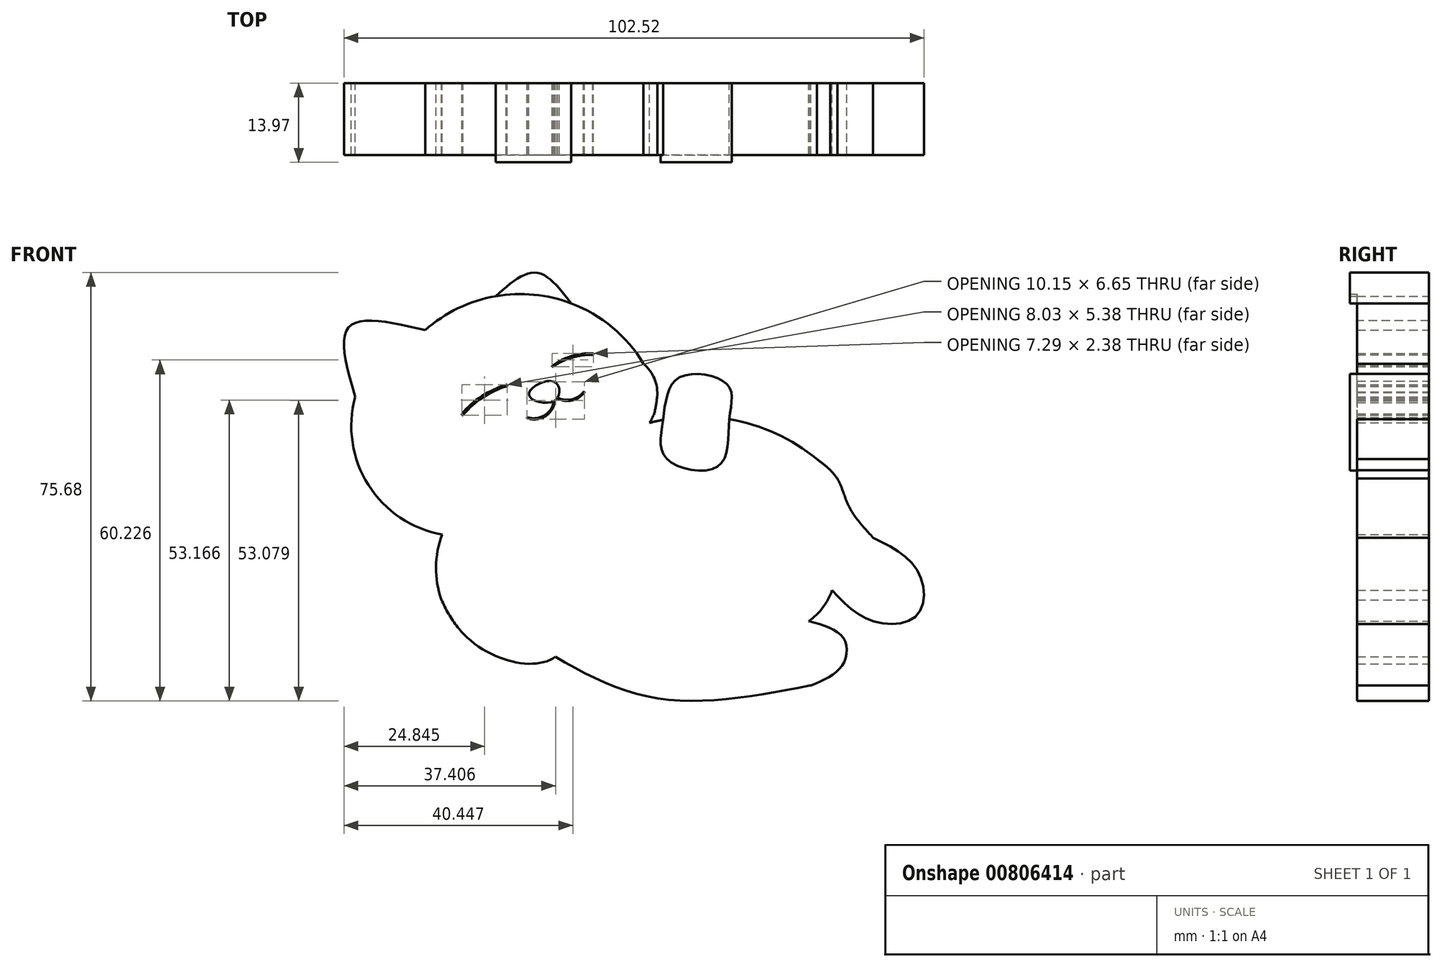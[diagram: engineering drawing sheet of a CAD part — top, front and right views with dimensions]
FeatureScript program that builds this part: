
annotation { "Feature Type Name" : "Feature", "Feature Type Description" : "" }
export const myFeature = defineFeature(function(context is Context, id is Id, definition is map)
    precondition{}
    {
        {
            var Q0;
            Q0=qCreatedBy(makeId("Front.planeOp"),FACE);
            var sketch = newSketch(context, id + "F0", { "sketchPlane" : qUnion([Q0])});
            skArc(sketch, "E0", {"start": v(56.76, -2.28) * mm, "mid": v(49.48, 2.28) * mm, "end": v(41.27, 4.8) * mm});
            skArc(sketch, "E1", {"start": v(59.42, -25.44) * mm, "mid": v(59.84, -24) * mm, "end": v(60.01, -22.52) * mm});
            skFitSpline(sketch, "E2", {"points": [v(55.5, -42.26) * mm, v(27.75, -44.4) * mm, v(5.04, -33.79) * mm], "startDerivative": vector(-56, -10.82) * mm, "endDerivative": vector(-44.82, 28.1) * mm});
            skFitSpline(sketch, "E3", {"points": [v(29.53, 4.68) * mm, v(30.27, -2.25) * mm, v(39.28, -3.51) * mm, v(41.27, 4.8) * mm, v(40.9, 10.9) * mm, v(32.43, 12.16) * mm, v(29.53, 4.68) * mm]});
            skArc(sketch, "E4", {"start": v(41.27, 4.8) * mm, "mid": v(35.37, 8.1) * mm, "end": v(29.53, 4.68) * mm});
            skPoint(sketch, "E5", {"position": v(-11.24, -21.98) * mm});
            skPoint(sketch, "E6", {"position": v(24.84, 3.42) * mm});
            skArc(sketch, "E7.trimOffspring", {"start": v(29.53, 4.68) * mm, "mid": v(27.16, 4.14) * mm, "end": v(24.84, 3.42) * mm});
            skPoint(sketch, "E8", {"position": v(6.4, -24.5) * mm});
            skPoint(sketch, "E9.3.internal.orphan", {"position": v(55.68, -42.26) * mm});
            skPoint(sketch, "E9.endDerivative.orphan", {"position": v(60.74, -44.4) * mm});
            skPoint(sketch, "E9.startDerivative.orphan", {"position": v(60.44, -32.16) * mm});
            skPoint(sketch, "E10.3.internal.orphan", {"position": v(66.67, -30.9) * mm});
            skFitSpline(sketch, "E11", {"points": [v(59.42, -25.44) * mm, v(66.67, -30.9) * mm, v(74.55, -29.7) * mm, v(74.55, -22.05) * mm, v(66.67, -16.13) * mm], "startDerivative": vector(25.1, -26.33) * mm, "endDerivative": vector(-35.3, 17.66) * mm});
            skFitSpline(sketch, "E12", {"points": [v(55.68, -42.26) * mm, v(61.18, -38.75) * mm, v(61.43, -33.9) * mm, v(54.9, -30.8) * mm], "startDerivative": vector(19.1, 8) * mm, "endDerivative": vector(-22.54, 5.93) * mm});
            skFitSpline(sketch, "E13", {"points": [v(66.67, -16.13) * mm, v(62.44, -10.72) * mm, v(60.34, -5.7) * mm, v(56.76, -2.28) * mm], "startDerivative": vector(-13.38, 14.34) * mm, "endDerivative": vector(-13.07, 9.95) * mm});
            skArc(sketch, "E14", {"start": v(62.44, -10.72) * mm, "mid": v(60.48, -5.9) * mm, "end": v(56.76, -2.28) * mm});
            skArc(sketch, "E15", {"start": v(52.98, -32.16) * mm, "mid": v(56.92, -29.5) * mm, "end": v(59.42, -25.44) * mm});
            skPoint(sketch, "E16.orphan", {"position": v(55.68, -30) * mm});
            skPoint(sketch, "E17", {"position": v(60.01, -22.52) * mm});
            skArc(sketch, "E18", {"start": v(-24.86, 8.73) * mm, "mid": v(-22.52, -6.83) * mm, "end": v(-9.46, -15.6) * mm});
            skFitSpline(sketch, "E19", {"points": [v(-24.86, 8.73) * mm, v(-25.93, 21.14) * mm, v(-12.5, 20.53) * mm], "startDerivative": vector(-9.2, 31.8) * mm, "endDerivative": vector(33.64, -7.95) * mm});
            skArc(sketch, "E20", {"start": v(17.84, 0) * mm, "mid": v(21.55, 1.28) * mm, "end": v(24.84, 3.42) * mm});
            skArc(sketch, "E21", {"start": v(28.49, 8.68) * mm, "mid": v(28.04, 11.94) * mm, "end": v(26.1, 14.6) * mm});
            skArc(sketch, "E22.trimOffspring", {"start": v(26.1, 14.6) * mm, "mid": v(8.19, 26.61) * mm, "end": v(-12.5, 20.53) * mm});
            skFitSpline(sketch, "E23", {"points": [v(28.49, 8.68) * mm, v(27.16, 4.14) * mm, v(16.83, -4.76) * mm], "startDerivative": vector(-1.19, -11.9) * mm, "endDerivative": vector(-20.46, -14.73) * mm});
            skPoint(sketch, "E24.0.internal.orphan", {"position": v(0, -25.5) * mm});
            skFitSpline(sketch, "E25.trimOffspring", {"points": [v(-9.46, -15.6) * mm, v(-11.24, -18.47) * mm, v(-5.05, -33.79) * mm, v(10.52, -37.17) * mm, v(12.32, -29.27) * mm, v(8.77, -26.58) * mm], "startDerivative": vector(-18.54, -16.44) * mm, "endDerivative": vector(-29.97, 11.85) * mm});
            skArc(sketch, "E26", {"start": v(-9.46, -15.6) * mm, "mid": v(-10.12, -25.39) * mm, "end": v(-5.05, -33.79) * mm});
            skPoint(sketch, "E27", {"position": v(1.82, 10.86) * mm});
            skArc(sketch, "E28", {"start": v(17.1, 16.44) * mm, "mid": v(13.36, 15.94) * mm, "end": v(9.99, 14.26) * mm});
            skArc(sketch, "E29", {"start": v(1.82, 10.86) * mm, "mid": v(-2.47, 8.88) * mm, "end": v(-6, 5.73) * mm});
            skFitSpline(sketch, "E30", {"points": [v(5.84, 9.15) * mm, v(10.25, 11.41) * mm, v(10.46, 8.12) * mm, v(5.84, 9.15) * mm]});
            skArc(sketch, "E31", {"start": v(5.53, 4.98) * mm, "mid": v(8.78, 5.33) * mm, "end": v(10.46, 8.12) * mm});
            skArc(sketch, "E32", {"start": v(10.83, 8.48) * mm, "mid": v(13.42, 8.1) * mm, "end": v(15.63, 9.5) * mm});
            skFitSpline(sketch, "E33", {"points": [v(0, 26.53) * mm, v(7.1, 30.68) * mm, v(13.3, 25.27) * mm], "startDerivative": vector(14.66, 13.08) * mm, "endDerivative": vector(11.94, -15.6) * mm});
            skLineSegment(sketch, "E34", {"start": v(55.5, -42.26) * mm, "end": v(55.68, -42.26) * mm});
            skArc(sketch, "E35", {"start": v(1.93, 10.6) * mm, "mid": v(-2.31, 8.63) * mm, "end": v(-5.8, 5.5) * mm});
            skArc(sketch, "E36", {"start": v(-6, 5.73) * mm, "mid": v(-5.97, 5.55) * mm, "end": v(-5.8, 5.5) * mm});
            skArc(sketch, "E37", {"start": v(17.13, 16.16) * mm, "mid": v(13.46, 15.68) * mm, "end": v(10.13, 14.06) * mm});
            skArc(sketch, "E38", {"start": v(9.99, 14.26) * mm, "mid": v(9.99, 14.1) * mm, "end": v(10.13, 14.06) * mm});
            skArc(sketch, "E39", {"start": v(17.13, 16.16) * mm, "mid": v(17.25, 16.32) * mm, "end": v(17.1, 16.44) * mm});
            skArc(sketch, "E40", {"start": v(1.93, 10.6) * mm, "mid": v(2, 10.8) * mm, "end": v(1.82, 10.86) * mm});
            skArc(sketch, "E41", {"start": v(5.57, 5.13) * mm, "mid": v(8.6, 5.5) * mm, "end": v(10.3, 8.03) * mm});
            skArc(sketch, "E42", {"start": v(5.57, 5.13) * mm, "mid": v(5.5, 5.07) * mm, "end": v(5.53, 4.98) * mm});
            skArc(sketch, "E43", {"start": v(10.9, 8.59) * mm, "mid": v(13.38, 8.3) * mm, "end": v(15.5, 9.6) * mm});
            skArc(sketch, "E44", {"start": v(15.63, 9.5) * mm, "mid": v(15.6, 9.61) * mm, "end": v(15.5, 9.6) * mm});
            skSolve(sketch);
        }
        {
            var Q0;
            Q0=makeQuery(id+"F0.imprint","IMPRINT",FACE,{"disambiguationData":[TD([[makeQuery(id+"F0.imprint","IMPRINT",EDGE,{"derivedFrom":sQuery(id+"F0.wireOp",EDGE,"E0")}),1.0]])]});
            extrude(context, id + "F1", {"entities" : qUnion([Q0]), "depth" : 12.7 * mm, "offsetDistance" : 25.4 * mm});
        }
        {
            var Q0;
            {var subQ0=sQuery(id+"F0.wireOp",EDGE,"E33");Q0=makeQuery(id+"F0.imprint","IMPRINT",FACE,{"disambiguationData":[TD([[makeQuery(id+"F0.imprint","IMPRINT",EDGE,{"derivedFrom":subQ0}),-1.0]])]});}
            var Q1;
            Q1=makeQuery(id+"F0.imprint","IMPRINT",FACE,{"disambiguationData":[TD([[makeQuery(id+"F0.imprint","IMPRINT",EDGE,{"derivedFrom":sQuery(id+"F0.wireOp",EDGE,"E3")}),1.0]])]});
            extrude(context, id + "F2", {"entities" : qUnion([Q0, Q1]), "operationType" : NewBodyOperationType.ADD, "depth" : 13.97 * mm, "offsetDistance" : 25.4 * mm});
        }
    });
